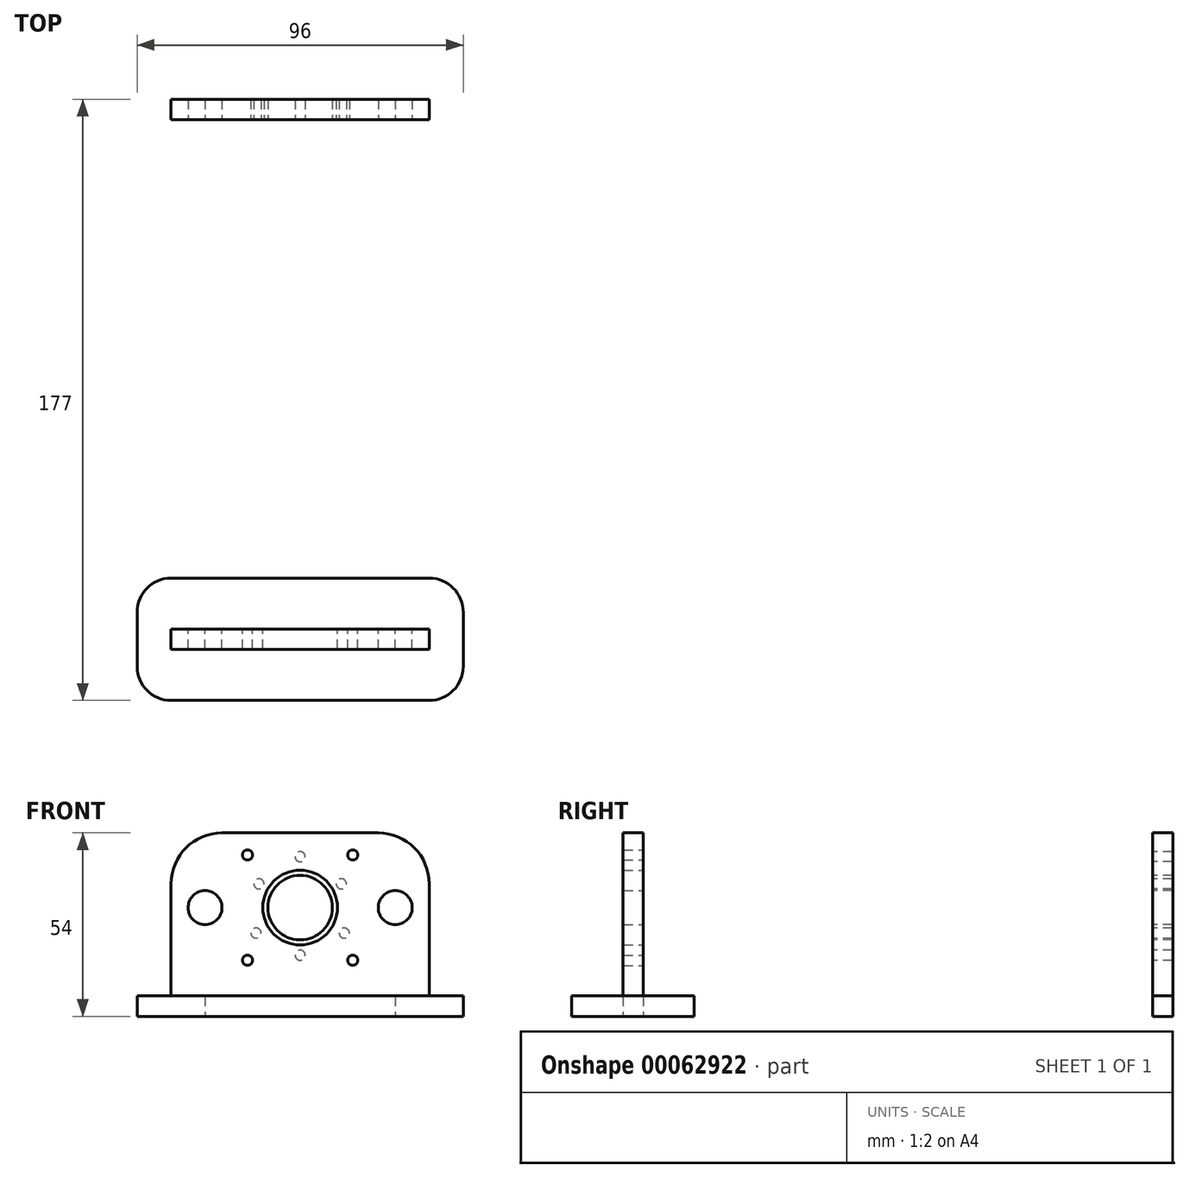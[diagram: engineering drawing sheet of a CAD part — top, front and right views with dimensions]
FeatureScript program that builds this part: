
annotation { "Feature Type Name" : "Feature", "Feature Type Description" : "" }
export const myFeature = defineFeature(function(context is Context, id is Id, definition is map)
    precondition{}
    {
        {
            var Q0;
            Q0=qCreatedBy(makeId("Front.planeOp"),FACE);
            var sketch = newSketch(context, id + "F0", { "sketchPlane" : qUnion([Q0])});
            skCircle(sketch, "E0", {"center": v(-28, 0) * mm, "radius": 5 * mm});
            skCircle(sketch, "E1", {"center": v(28, 0) * mm, "radius": 5 * mm});
            skLineSegment(sketch, "E2", {"start": v(-28, 0) * mm, "end": v(28, 0) * mm, "construction": true});
            skLineSegment(sketch, "E3", {"start": v(-15.5, 15.5) * mm, "end": v(15.5, -15.5) * mm, "construction": true});
            skLineSegment(sketch, "E4", {"start": v(-15.5, -15.5) * mm, "end": v(15.5, 15.5) * mm, "construction": true});
            skPoint(sketch, "E5", {"position": v(0, 0) * mm});
            skCircle(sketch, "E6", {"center": v(0, 0) * mm, "radius": 11 * mm});
            skCircle(sketch, "E7", {"center": v(-15.5, 15.5) * mm, "radius": 1.5 * mm});
            skCircle(sketch, "E8", {"center": v(15.5, 15.5) * mm, "radius": 1.5 * mm});
            skCircle(sketch, "E9", {"center": v(15.5, -15.5) * mm, "radius": 1.5 * mm});
            skCircle(sketch, "E10", {"center": v(-15.5, -15.5) * mm, "radius": 1.5 * mm});
            skLineSegment(sketch, "E11.bottom", {"start": v(-23, 22) * mm, "end": v(23, 22) * mm});
            skLineSegment(sketch, "E11.top", {"start": v(-28, -32) * mm, "end": v(28, -32) * mm});
            skLineSegment(sketch, "E11.left", {"start": v(-38, 7) * mm, "end": v(-38, -26) * mm});
            skLineSegment(sketch, "E11.right", {"start": v(38, 7) * mm, "end": v(38, -26) * mm});
            skPoint(sketch, "E12.visualSharp", {"position": v(-38, 22) * mm});
            skArc(sketch, "E12.filletArc", {"start": v(-23, 22) * mm, "mid": v(-33.6, 17.6) * mm, "end": v(-38, 7) * mm});
            skPoint(sketch, "E13.visualSharp", {"position": v(38, 22) * mm});
            skArc(sketch, "E13.filletArc", {"start": v(38, 7) * mm, "mid": v(33.6, 17.6) * mm, "end": v(23, 22) * mm});
            skLineSegment(sketch, "E14.top", {"start": v(-38, -26) * mm, "end": v(-28, -26) * mm});
            skLineSegment(sketch, "E14.right", {"start": v(-28, -32) * mm, "end": v(-28, -26) * mm});
            skLineSegment(sketch, "E15.top", {"start": v(38, -26) * mm, "end": v(28, -26) * mm});
            skLineSegment(sketch, "E15.right", {"start": v(28, -32) * mm, "end": v(28, -26) * mm});
            skSolve(sketch);
        }
        {
            var Q0;
            Q0 = qSketchRegion(id + "F0", true);
            extrude(context, id + "F1", {"entities" : qUnion([Q0]), "depth" : 6 * mm});
        }
        {
            var Q0;
            Q0=makeQuery(id+"F1.opExtrude","CAP_FACE",FACE,{"disambiguationData":[OSD([sQuery(id+"F0.wireOp",EDGE,"E0"),sQuery(id+"F0.wireOp",EDGE,"E1"),sQuery(id+"F0.wireOp",EDGE,"E6"),sQuery(id+"F0.wireOp",EDGE,"E7"),sQuery(id+"F0.wireOp",EDGE,"E8"),sQuery(id+"F0.wireOp",EDGE,"E9"),sQuery(id+"F0.wireOp",EDGE,"E10"),sQuery(id+"F0.wireOp",EDGE,"E11.bottom"),sQuery(id+"F0.wireOp",EDGE,"E11.top"),sQuery(id+"F0.wireOp",EDGE,"E11.left"),sQuery(id+"F0.wireOp",EDGE,"E11.right"),sQuery(id+"F0.wireOp",EDGE,"E12.filletArc"),sQuery(id+"F0.wireOp",EDGE,"E13.filletArc"),sQuery(id+"F0.wireOp",EDGE,"E14.top"),sQuery(id+"F0.wireOp",EDGE,"E14.right"),sQuery(id+"F0.wireOp",EDGE,"E15.top"),sQuery(id+"F0.wireOp",EDGE,"E15.right")])],"isStart":true});
            cPlane(context, id + "F2", {"entities" : qUnion([Q0]), "cplaneType" : CPlaneType.OFFSET, "offset" : 150 * mm, "width" : 150 * mm, "height" : 150 * mm});
        }
        {
            var Q0;
            Q0=qCreatedBy(id+"F2.planeOp",FACE);
            var sketch = newSketch(context, id + "F3", { "sketchPlane" : qUnion([Q0])});
            skLineSegment(sketch, "E16.5", {"start": v(0, 15) * mm, "end": v(13, 7.5) * mm, "construction": true});
            skLineSegment(sketch, "E16.4", {"start": v(-13, 7.5) * mm, "end": v(0, 15) * mm, "construction": true});
            skLineSegment(sketch, "E16.3", {"start": v(-13, -7.5) * mm, "end": v(-13, 7.5) * mm, "construction": true});
            skLineSegment(sketch, "E16.2", {"start": v(0, -15) * mm, "end": v(-13, -7.5) * mm, "construction": true});
            skLineSegment(sketch, "E16.1", {"start": v(13, -7.5) * mm, "end": v(0, -15) * mm, "construction": true});
            skLineSegment(sketch, "E16.0", {"start": v(13, 7.5) * mm, "end": v(13, -7.5) * mm, "construction": true});
            skCircle(sketch, "E16.cCircle", {"center": v(0, 0) * mm, "radius": 15 * mm, "construction": true});
            skCircle(sketch, "E17", {"center": v(0, 0) * mm, "radius": 14 * mm, "construction": true});
            skCircle(sketch, "E18", {"center": v(0, 0) * mm, "radius": 9.5 * mm});
            skLineSegment(sketch, "E19", {"start": v(-28, 0) * mm, "end": v(28, 0) * mm, "construction": true});
            skCircle(sketch, "E20", {"center": v(28, 0) * mm, "radius": 5 * mm});
            skCircle(sketch, "E21", {"center": v(-28, 0) * mm, "radius": 5 * mm});
            skLineSegment(sketch, "E22", {"start": v(0, 15) * mm, "end": v(0, -15) * mm, "construction": true});
            skLineSegment(sketch, "E23", {"start": v(13, -7.5) * mm, "end": v(-13, 7.5) * mm, "construction": true});
            skLineSegment(sketch, "E24", {"start": v(13, 7.5) * mm, "end": v(-13, -7.5) * mm, "construction": true});
            skCircle(sketch, "E25", {"center": v(-12.12, 7) * mm, "radius": 1.5 * mm});
            skCircle(sketch, "E26", {"center": v(-13, -7.5) * mm, "radius": 1.5 * mm});
            skCircle(sketch, "E27", {"center": v(0, -14) * mm, "radius": 1.5 * mm});
            skCircle(sketch, "E28", {"center": v(13, -7.5) * mm, "radius": 1.5 * mm});
            skCircle(sketch, "E29", {"center": v(12.12, 7) * mm, "radius": 1.5 * mm});
            skCircle(sketch, "E30", {"center": v(0, 15) * mm, "radius": 1.5 * mm});
            skLineSegment(sketch, "E31.bottom", {"start": v(-38, -26) * mm, "end": v(-28, -26) * mm});
            skLineSegment(sketch, "E31.top", {"start": v(-23, 22) * mm, "end": v(23, 22) * mm});
            skLineSegment(sketch, "E31.left", {"start": v(-38, -26) * mm, "end": v(-38, 7) * mm});
            skLineSegment(sketch, "E31.right", {"start": v(38, -26) * mm, "end": v(38, 7) * mm});
            skLineSegment(sketch, "E32.top", {"start": v(-28, -32) * mm, "end": v(28, -32) * mm});
            skLineSegment(sketch, "E32.left", {"start": v(-28, -26) * mm, "end": v(-28, -32) * mm});
            skLineSegment(sketch, "E32.right", {"start": v(28, -26) * mm, "end": v(28, -32) * mm});
            skPoint(sketch, "E33.visualSharp", {"position": v(38, 22) * mm});
            skArc(sketch, "E33.filletArc", {"start": v(38, 7) * mm, "mid": v(33.6, 17.6) * mm, "end": v(23, 22) * mm});
            skPoint(sketch, "E34.visualSharp", {"position": v(-38, 22) * mm});
            skArc(sketch, "E34.filletArc", {"start": v(-23, 22) * mm, "mid": v(-33.6, 17.6) * mm, "end": v(-38, 7) * mm});
            skLineSegment(sketch, "E35.trimOffspring", {"start": v(28, -26) * mm, "end": v(38, -26) * mm});
            skSolve(sketch);
        }
        {
            var Q0;
            Q0 = qSketchRegion(id + "F3", true);
            extrude(context, id + "F4", {"entities" : qUnion([Q0]), "depth" : 6 * mm});
        }
        {
            var Q0;
            Q0=makeQuery(id+"F1.opExtrude","SWEPT_FACE",FACE,{"disambiguationData":[OSD([sQuery(id+"F0.wireOp",EDGE,"E11.top")])]});
            var sketch = newSketch(context, id + "F5", { "sketchPlane" : qUnion([Q0])});
            skLineSegment(sketch, "E36.bottom", {"start": v(38, 21) * mm, "end": v(-38, 21) * mm});
            skLineSegment(sketch, "E36.top", {"start": v(38, -15) * mm, "end": v(-38, -15) * mm});
            skLineSegment(sketch, "E36.left", {"start": v(48, 11) * mm, "end": v(48, -5) * mm});
            skLineSegment(sketch, "E36.right", {"start": v(-48, 11) * mm, "end": v(-48, -5) * mm});
            skLineSegment(sketch, "E37.bottom", {"start": v(28, 6) * mm, "end": v(-28, 6) * mm});
            skLineSegment(sketch, "E37.top", {"start": v(28, 0) * mm, "end": v(-28, 0) * mm});
            skLineSegment(sketch, "E37.left", {"start": v(28, 6) * mm, "end": v(28, 0) * mm});
            skLineSegment(sketch, "E37.right", {"start": v(-28, 6) * mm, "end": v(-28, 0) * mm});
            skPoint(sketch, "E38.visualSharp", {"position": v(-48, 21) * mm});
            skArc(sketch, "E38.filletArc", {"start": v(-38, 21) * mm, "mid": v(-45.07, 18.07) * mm, "end": v(-48, 11) * mm});
            skPoint(sketch, "E39.visualSharp", {"position": v(48, 21) * mm});
            skArc(sketch, "E39.filletArc", {"start": v(48, 11) * mm, "mid": v(45.07, 18.07) * mm, "end": v(38, 21) * mm});
            skPoint(sketch, "E40.visualSharp", {"position": v(48, -15) * mm});
            skArc(sketch, "E40.filletArc", {"start": v(38, -15) * mm, "mid": v(45.07, -12.07) * mm, "end": v(48, -5) * mm});
            skPoint(sketch, "E41.visualSharp", {"position": v(-48, -15) * mm});
            skArc(sketch, "E41.filletArc", {"start": v(-48, -5) * mm, "mid": v(-45.07, -12.07) * mm, "end": v(-38, -15) * mm});
            skSolve(sketch);
        }
        {
            var Q0;
            Q0 = qSketchRegion(id + "F5", true);
            extrude(context, id + "F6", {"entities" : qUnion([Q0]), "oppositeDirection" : true, "depth" : 6 * mm});
        }
    });
